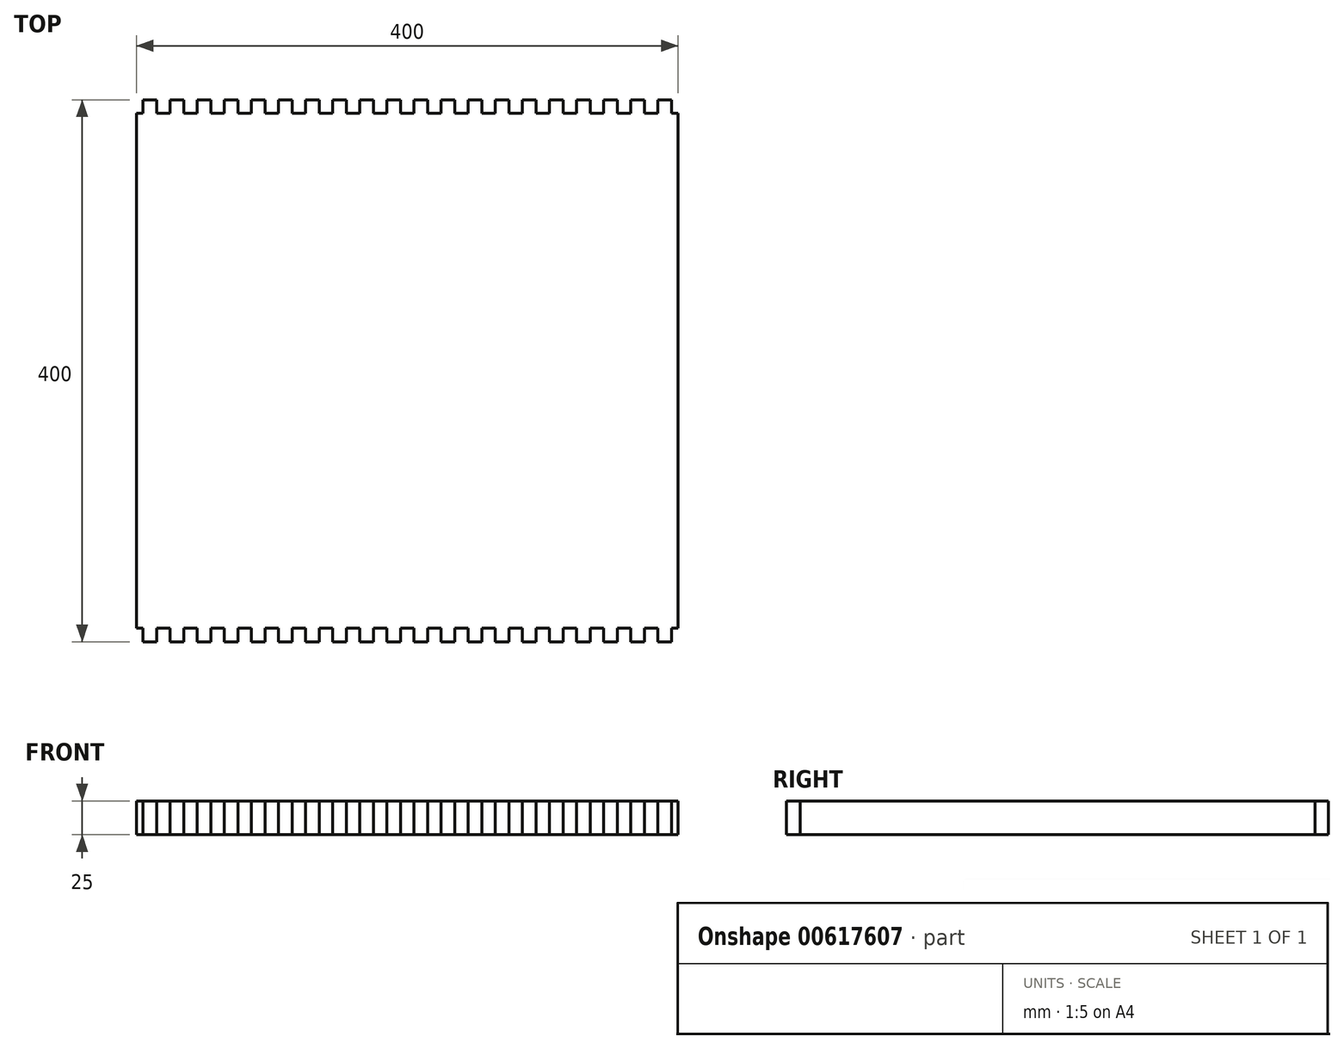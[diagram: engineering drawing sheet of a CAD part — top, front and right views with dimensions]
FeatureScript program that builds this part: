
annotation { "Feature Type Name" : "Feature", "Feature Type Description" : "" }
export const myFeature = defineFeature(function(context is Context, id is Id, definition is map)
    precondition{}
    {
        {
            var Q0;
            Q0=qCreatedBy(makeId("Top.planeOp"),FACE);
            var sketch = newSketch(context, id + "F0", { "sketchPlane" : qUnion([Q0])});
            skLineSegment(sketch, "E0.bottom", {"start": v(200, -200) * mm, "end": v(-200, -200) * mm});
            skLineSegment(sketch, "E0.top", {"start": v(200, 200) * mm, "end": v(-200, 200) * mm});
            skLineSegment(sketch, "E0.left", {"start": v(200, -200) * mm, "end": v(200, 200) * mm});
            skLineSegment(sketch, "E0.right", {"start": v(-200, -200) * mm, "end": v(-200, 200) * mm});
            skPoint(sketch, "E0.middle", {"position": v(0, 0) * mm});
            skLineSegment(sketch, "E1", {"start": v(0, -200) * mm, "end": v(-5, -200) * mm});
            skLineSegment(sketch, "E2.bottom", {"start": v(-5, -200) * mm, "end": v(5, -200) * mm});
            skLineSegment(sketch, "E2.top", {"start": v(-5, -190) * mm, "end": v(5, -190) * mm});
            skLineSegment(sketch, "E2.left", {"start": v(-5, -200) * mm, "end": v(-5, -190) * mm});
            skLineSegment(sketch, "E2.right", {"start": v(5, -200) * mm, "end": v(5, -190) * mm});
            skLineSegment(sketch, "E3.1.0.0", {"start": v(15, -190) * mm, "end": v(25, -190) * mm});
            skLineSegment(sketch, "E3.1.0.1", {"start": v(15, -200) * mm, "end": v(15, -190) * mm});
            skLineSegment(sketch, "E3.1.0.2", {"start": v(25, -200) * mm, "end": v(25, -190) * mm});
            skLineSegment(sketch, "E3.1.0.3", {"start": v(15, -200) * mm, "end": v(25, -200) * mm});
            skLineSegment(sketch, "E3.2.0.0", {"start": v(35, -190) * mm, "end": v(45, -190) * mm});
            skLineSegment(sketch, "E3.2.0.1", {"start": v(35, -200) * mm, "end": v(35, -190) * mm});
            skLineSegment(sketch, "E3.2.0.2", {"start": v(45, -200) * mm, "end": v(45, -190) * mm});
            skLineSegment(sketch, "E3.2.0.3", {"start": v(35, -200) * mm, "end": v(45, -200) * mm});
            skLineSegment(sketch, "E3.3.0.0", {"start": v(55, -190) * mm, "end": v(65, -190) * mm});
            skLineSegment(sketch, "E3.3.0.1", {"start": v(55, -200) * mm, "end": v(55, -190) * mm});
            skLineSegment(sketch, "E3.3.0.2", {"start": v(65, -200) * mm, "end": v(65, -190) * mm});
            skLineSegment(sketch, "E3.3.0.3", {"start": v(55, -200) * mm, "end": v(65, -200) * mm});
            skLineSegment(sketch, "E3.4.0.0", {"start": v(75, -190) * mm, "end": v(85, -190) * mm});
            skLineSegment(sketch, "E3.4.0.1", {"start": v(75, -200) * mm, "end": v(75, -190) * mm});
            skLineSegment(sketch, "E3.4.0.2", {"start": v(85, -200) * mm, "end": v(85, -190) * mm});
            skLineSegment(sketch, "E3.4.0.3", {"start": v(75, -200) * mm, "end": v(85, -200) * mm});
            skLineSegment(sketch, "E3.5.0.0", {"start": v(95, -190) * mm, "end": v(105, -190) * mm});
            skLineSegment(sketch, "E3.5.0.1", {"start": v(95, -200) * mm, "end": v(95, -190) * mm});
            skLineSegment(sketch, "E3.5.0.2", {"start": v(105, -200) * mm, "end": v(105, -190) * mm});
            skLineSegment(sketch, "E3.5.0.3", {"start": v(95, -200) * mm, "end": v(105, -200) * mm});
            skLineSegment(sketch, "E3.6.0.0", {"start": v(115, -190) * mm, "end": v(125, -190) * mm});
            skLineSegment(sketch, "E3.6.0.1", {"start": v(115, -200) * mm, "end": v(115, -190) * mm});
            skLineSegment(sketch, "E3.6.0.2", {"start": v(125, -200) * mm, "end": v(125, -190) * mm});
            skLineSegment(sketch, "E3.6.0.3", {"start": v(115, -200) * mm, "end": v(125, -200) * mm});
            skLineSegment(sketch, "E3.7.0.0", {"start": v(135, -190) * mm, "end": v(145, -190) * mm});
            skLineSegment(sketch, "E3.7.0.1", {"start": v(135, -200) * mm, "end": v(135, -190) * mm});
            skLineSegment(sketch, "E3.7.0.2", {"start": v(145, -200) * mm, "end": v(145, -190) * mm});
            skLineSegment(sketch, "E3.7.0.3", {"start": v(135, -200) * mm, "end": v(145, -200) * mm});
            skLineSegment(sketch, "E3.8.0.0", {"start": v(155, -190) * mm, "end": v(165, -190) * mm});
            skLineSegment(sketch, "E3.8.0.1", {"start": v(155, -200) * mm, "end": v(155, -190) * mm});
            skLineSegment(sketch, "E3.8.0.2", {"start": v(165, -200) * mm, "end": v(165, -190) * mm});
            skLineSegment(sketch, "E3.8.0.3", {"start": v(155, -200) * mm, "end": v(165, -200) * mm});
            skLineSegment(sketch, "E3.9.0.0", {"start": v(175, -190) * mm, "end": v(185, -190) * mm});
            skLineSegment(sketch, "E3.9.0.1", {"start": v(175, -200) * mm, "end": v(175, -190) * mm});
            skLineSegment(sketch, "E3.9.0.2", {"start": v(185, -200) * mm, "end": v(185, -190) * mm});
            skLineSegment(sketch, "E3.9.0.3", {"start": v(175, -200) * mm, "end": v(185, -200) * mm});
            skLineSegment(sketch, "E3.10.0.0", {"start": v(195, -190) * mm, "end": v(205, -190) * mm});
            skLineSegment(sketch, "E3.10.0.1", {"start": v(195, -200) * mm, "end": v(195, -190) * mm});
            skLineSegment(sketch, "E3.10.0.2", {"start": v(205, -200) * mm, "end": v(205, -190) * mm});
            skLineSegment(sketch, "E3.10.0.3", {"start": v(195, -200) * mm, "end": v(205, -200) * mm});
            skLineSegment(sketch, "E4.1.0.0", {"start": v(-25, -200) * mm, "end": v(-25, -190) * mm});
            skLineSegment(sketch, "E4.1.0.1", {"start": v(-25, -190) * mm, "end": v(-15, -190) * mm});
            skLineSegment(sketch, "E4.1.0.2", {"start": v(-15, -200) * mm, "end": v(-15, -190) * mm});
            skLineSegment(sketch, "E4.1.0.3", {"start": v(-25, -200) * mm, "end": v(-15, -200) * mm});
            skLineSegment(sketch, "E4.2.0.0", {"start": v(-45, -200) * mm, "end": v(-45, -190) * mm});
            skLineSegment(sketch, "E4.2.0.1", {"start": v(-45, -190) * mm, "end": v(-35, -190) * mm});
            skLineSegment(sketch, "E4.2.0.2", {"start": v(-35, -200) * mm, "end": v(-35, -190) * mm});
            skLineSegment(sketch, "E4.2.0.3", {"start": v(-45, -200) * mm, "end": v(-35, -200) * mm});
            skLineSegment(sketch, "E4.3.0.0", {"start": v(-65, -200) * mm, "end": v(-65, -190) * mm});
            skLineSegment(sketch, "E4.3.0.1", {"start": v(-65, -190) * mm, "end": v(-55, -190) * mm});
            skLineSegment(sketch, "E4.3.0.2", {"start": v(-55, -200) * mm, "end": v(-55, -190) * mm});
            skLineSegment(sketch, "E4.3.0.3", {"start": v(-65, -200) * mm, "end": v(-55, -200) * mm});
            skLineSegment(sketch, "E4.4.0.0", {"start": v(-85, -200) * mm, "end": v(-85, -190) * mm});
            skLineSegment(sketch, "E4.4.0.1", {"start": v(-85, -190) * mm, "end": v(-75, -190) * mm});
            skLineSegment(sketch, "E4.4.0.2", {"start": v(-75, -200) * mm, "end": v(-75, -190) * mm});
            skLineSegment(sketch, "E4.4.0.3", {"start": v(-85, -200) * mm, "end": v(-75, -200) * mm});
            skLineSegment(sketch, "E4.5.0.0", {"start": v(-105, -200) * mm, "end": v(-105, -190) * mm});
            skLineSegment(sketch, "E4.5.0.1", {"start": v(-105, -190) * mm, "end": v(-95, -190) * mm});
            skLineSegment(sketch, "E4.5.0.2", {"start": v(-95, -200) * mm, "end": v(-95, -190) * mm});
            skLineSegment(sketch, "E4.5.0.3", {"start": v(-105, -200) * mm, "end": v(-95, -200) * mm});
            skLineSegment(sketch, "E4.6.0.0", {"start": v(-125, -200) * mm, "end": v(-125, -190) * mm});
            skLineSegment(sketch, "E4.6.0.1", {"start": v(-125, -190) * mm, "end": v(-115, -190) * mm});
            skLineSegment(sketch, "E4.6.0.2", {"start": v(-115, -200) * mm, "end": v(-115, -190) * mm});
            skLineSegment(sketch, "E4.6.0.3", {"start": v(-125, -200) * mm, "end": v(-115, -200) * mm});
            skLineSegment(sketch, "E4.7.0.0", {"start": v(-145, -200) * mm, "end": v(-145, -190) * mm});
            skLineSegment(sketch, "E4.7.0.1", {"start": v(-145, -190) * mm, "end": v(-135, -190) * mm});
            skLineSegment(sketch, "E4.7.0.2", {"start": v(-135, -200) * mm, "end": v(-135, -190) * mm});
            skLineSegment(sketch, "E4.7.0.3", {"start": v(-145, -200) * mm, "end": v(-135, -200) * mm});
            skLineSegment(sketch, "E4.8.0.0", {"start": v(-165, -200) * mm, "end": v(-165, -190) * mm});
            skLineSegment(sketch, "E4.8.0.1", {"start": v(-165, -190) * mm, "end": v(-155, -190) * mm});
            skLineSegment(sketch, "E4.8.0.2", {"start": v(-155, -200) * mm, "end": v(-155, -190) * mm});
            skLineSegment(sketch, "E4.8.0.3", {"start": v(-165, -200) * mm, "end": v(-155, -200) * mm});
            skLineSegment(sketch, "E4.9.0.0", {"start": v(-185, -200) * mm, "end": v(-185, -190) * mm});
            skLineSegment(sketch, "E4.9.0.1", {"start": v(-185, -190) * mm, "end": v(-175, -190) * mm});
            skLineSegment(sketch, "E4.9.0.2", {"start": v(-175, -200) * mm, "end": v(-175, -190) * mm});
            skLineSegment(sketch, "E4.9.0.3", {"start": v(-185, -200) * mm, "end": v(-175, -200) * mm});
            skLineSegment(sketch, "E4.10.0.0", {"start": v(-205, -200) * mm, "end": v(-205, -190) * mm});
            skLineSegment(sketch, "E4.10.0.1", {"start": v(-205, -190) * mm, "end": v(-195, -190) * mm});
            skLineSegment(sketch, "E4.10.0.2", {"start": v(-195, -200) * mm, "end": v(-195, -190) * mm});
            skLineSegment(sketch, "E4.10.0.3", {"start": v(-205, -200) * mm, "end": v(-195, -200) * mm});
            skLineSegment(sketch, "E4.direction1", {"start": v(-5, -200) * mm, "end": v(-25, -200) * mm, "construction": true});
            skLineSegment(sketch, "E5.MirrorCS", {"start": v(-135, 200) * mm, "end": v(-135, 190) * mm});
            skLineSegment(sketch, "E6.MirrorCS", {"start": v(-125, 200) * mm, "end": v(-115, 200) * mm});
            skLineSegment(sketch, "E7.MirrorCS", {"start": v(-105, 200) * mm, "end": v(-105, 190) * mm});
            skLineSegment(sketch, "E8.MirrorCS", {"start": v(-55, 200) * mm, "end": v(-55, 190) * mm});
            skLineSegment(sketch, "E9.MirrorCS", {"start": v(-25, 200) * mm, "end": v(-25, 190) * mm});
            skLineSegment(sketch, "E10.MirrorCS", {"start": v(-145, 200) * mm, "end": v(-145, 190) * mm});
            skLineSegment(sketch, "E11.MirrorCS", {"start": v(-65, 200) * mm, "end": v(-65, 190) * mm});
            skLineSegment(sketch, "E12.MirrorCS", {"start": v(75, 200) * mm, "end": v(85, 200) * mm});
            skLineSegment(sketch, "E13.MirrorCS", {"start": v(-105, 190) * mm, "end": v(-95, 190) * mm});
            skLineSegment(sketch, "E14.MirrorCS", {"start": v(185, 200) * mm, "end": v(185, 190) * mm});
            skLineSegment(sketch, "E15.MirrorCS", {"start": v(-25, 190) * mm, "end": v(-15, 190) * mm});
            skLineSegment(sketch, "E16.MirrorCS", {"start": v(-85, 190) * mm, "end": v(-75, 190) * mm});
            skLineSegment(sketch, "E17.MirrorCS", {"start": v(195, 200) * mm, "end": v(195, 190) * mm});
            skLineSegment(sketch, "E18.MirrorCS", {"start": v(105, 200) * mm, "end": v(105, 190) * mm});
            skLineSegment(sketch, "E19.MirrorCS", {"start": v(135, 200) * mm, "end": v(135, 190) * mm});
            skLineSegment(sketch, "E20.MirrorCS", {"start": v(155, 200) * mm, "end": v(155, 190) * mm});
            skLineSegment(sketch, "E21.MirrorCS", {"start": v(-45, 190) * mm, "end": v(-35, 190) * mm});
            skLineSegment(sketch, "E22.MirrorCS", {"start": v(55, 200) * mm, "end": v(65, 200) * mm});
            skLineSegment(sketch, "E23.MirrorCS", {"start": v(75, 200) * mm, "end": v(75, 190) * mm});
            skLineSegment(sketch, "E24.MirrorCS", {"start": v(-125, 190) * mm, "end": v(-115, 190) * mm});
            skLineSegment(sketch, "E25.MirrorCS", {"start": v(-165, 200) * mm, "end": v(-165, 190) * mm});
            skLineSegment(sketch, "E26.MirrorCS", {"start": v(175, 200) * mm, "end": v(175, 190) * mm});
            skLineSegment(sketch, "E27.MirrorCS", {"start": v(-155, 200) * mm, "end": v(-155, 190) * mm});
            skLineSegment(sketch, "E28.MirrorCS", {"start": v(-105, 200) * mm, "end": v(-95, 200) * mm});
            skLineSegment(sketch, "E29.MirrorCS", {"start": v(-75, 200) * mm, "end": v(-75, 190) * mm});
            skLineSegment(sketch, "E30.MirrorCS", {"start": v(-85, 200) * mm, "end": v(-85, 190) * mm});
            skLineSegment(sketch, "E31.MirrorCS", {"start": v(125, 200) * mm, "end": v(125, 190) * mm});
            skLineSegment(sketch, "E32.MirrorCS", {"start": v(-25, 200) * mm, "end": v(-15, 200) * mm});
            skLineSegment(sketch, "E33.MirrorCS", {"start": v(135, 200) * mm, "end": v(145, 200) * mm});
            skLineSegment(sketch, "E34.MirrorCS", {"start": v(-35, 200) * mm, "end": v(-35, 190) * mm});
            skLineSegment(sketch, "E35.MirrorCS", {"start": v(165, 200) * mm, "end": v(165, 190) * mm});
            skLineSegment(sketch, "E36.MirrorCS", {"start": v(85, 200) * mm, "end": v(85, 190) * mm});
            skLineSegment(sketch, "E37.MirrorCS", {"start": v(-115, 200) * mm, "end": v(-115, 190) * mm});
            skLineSegment(sketch, "E38.MirrorCS", {"start": v(-85, 200) * mm, "end": v(-75, 200) * mm});
            skLineSegment(sketch, "E39.MirrorCS", {"start": v(-65, 190) * mm, "end": v(-55, 190) * mm});
            skLineSegment(sketch, "E40.MirrorCS", {"start": v(55, 200) * mm, "end": v(55, 190) * mm});
            skLineSegment(sketch, "E41.MirrorCS", {"start": v(-5, 200) * mm, "end": v(5, 200) * mm});
            skLineSegment(sketch, "E42.MirrorCS", {"start": v(0, 200) * mm, "end": v(-5, 200) * mm});
            skLineSegment(sketch, "E43.MirrorCS", {"start": v(-145, 190) * mm, "end": v(-135, 190) * mm});
            skLineSegment(sketch, "E44.MirrorCS", {"start": v(-125, 200) * mm, "end": v(-125, 190) * mm});
            skLineSegment(sketch, "E45.MirrorCS", {"start": v(155, 190) * mm, "end": v(165, 190) * mm});
            skLineSegment(sketch, "E46.MirrorCS", {"start": v(75, 190) * mm, "end": v(85, 190) * mm});
            skLineSegment(sketch, "E47.MirrorCS", {"start": v(-45, 200) * mm, "end": v(-45, 190) * mm});
            skLineSegment(sketch, "E48.MirrorCS", {"start": v(55, 190) * mm, "end": v(65, 190) * mm});
            skLineSegment(sketch, "E49.MirrorCS", {"start": v(-185, 200) * mm, "end": v(-185, 190) * mm});
            skLineSegment(sketch, "E50.MirrorCS", {"start": v(-65, 200) * mm, "end": v(-55, 200) * mm});
            skLineSegment(sketch, "E51.MirrorCS", {"start": v(-95, 200) * mm, "end": v(-95, 190) * mm});
            skLineSegment(sketch, "E52.MirrorCS", {"start": v(175, 200) * mm, "end": v(185, 200) * mm});
            skLineSegment(sketch, "E53.MirrorCS", {"start": v(-15, 200) * mm, "end": v(-15, 190) * mm});
            skLineSegment(sketch, "E54.MirrorCS", {"start": v(145, 200) * mm, "end": v(145, 190) * mm});
            skLineSegment(sketch, "E55.MirrorCS", {"start": v(95, 200) * mm, "end": v(105, 200) * mm});
            skLineSegment(sketch, "E56.MirrorCS", {"start": v(-5, 200) * mm, "end": v(-5, 190) * mm});
            skLineSegment(sketch, "E57.MirrorCS", {"start": v(135, 190) * mm, "end": v(145, 190) * mm});
            skLineSegment(sketch, "E58.MirrorCS", {"start": v(-5, 200) * mm, "end": v(-25, 200) * mm, "construction": true});
            skLineSegment(sketch, "E59.MirrorCS", {"start": v(95, 190) * mm, "end": v(105, 190) * mm});
            skLineSegment(sketch, "E60.MirrorCS", {"start": v(175, 190) * mm, "end": v(185, 190) * mm});
            skLineSegment(sketch, "E61.MirrorCS", {"start": v(-145, 200) * mm, "end": v(-135, 200) * mm});
            skLineSegment(sketch, "E62.MirrorCS", {"start": v(25, 200) * mm, "end": v(25, 190) * mm});
            skLineSegment(sketch, "E63.MirrorCS", {"start": v(-45, 200) * mm, "end": v(-35, 200) * mm});
            skLineSegment(sketch, "E64.MirrorCS", {"start": v(65, 200) * mm, "end": v(65, 190) * mm});
            skLineSegment(sketch, "E65.MirrorCS", {"start": v(155, 200) * mm, "end": v(165, 200) * mm});
            skLineSegment(sketch, "E66.MirrorCS", {"start": v(95, 200) * mm, "end": v(95, 190) * mm});
            skLineSegment(sketch, "E67.MirrorCS", {"start": v(-5, 190) * mm, "end": v(5, 190) * mm});
            skLineSegment(sketch, "E68.MirrorCS", {"start": v(35, 200) * mm, "end": v(35, 190) * mm});
            skLineSegment(sketch, "E69.MirrorCS", {"start": v(-165, 190) * mm, "end": v(-155, 190) * mm});
            skLineSegment(sketch, "E70.MirrorCS", {"start": v(115, 200) * mm, "end": v(115, 190) * mm});
            skLineSegment(sketch, "E71.MirrorCS", {"start": v(45, 200) * mm, "end": v(45, 190) * mm});
            skLineSegment(sketch, "E72.MirrorCS", {"start": v(-185, 200) * mm, "end": v(-175, 200) * mm});
            skLineSegment(sketch, "E73.MirrorCS", {"start": v(195, 190) * mm, "end": v(205, 190) * mm});
            skLineSegment(sketch, "E74.MirrorCS", {"start": v(115, 190) * mm, "end": v(125, 190) * mm});
            skLineSegment(sketch, "E75.MirrorCS", {"start": v(-185, 190) * mm, "end": v(-175, 190) * mm});
            skLineSegment(sketch, "E76.MirrorCS", {"start": v(35, 200) * mm, "end": v(45, 200) * mm});
            skLineSegment(sketch, "E77.MirrorCS", {"start": v(-165, 200) * mm, "end": v(-155, 200) * mm});
            skLineSegment(sketch, "E78.MirrorCS", {"start": v(115, 200) * mm, "end": v(125, 200) * mm});
            skLineSegment(sketch, "E79.MirrorCS", {"start": v(-175, 200) * mm, "end": v(-175, 190) * mm});
            skLineSegment(sketch, "E80.MirrorCS", {"start": v(15, 200) * mm, "end": v(15, 190) * mm});
            skLineSegment(sketch, "E81.MirrorCS", {"start": v(15, 190) * mm, "end": v(25, 190) * mm});
            skLineSegment(sketch, "E82.MirrorCS", {"start": v(5, 200) * mm, "end": v(5, 190) * mm});
            skLineSegment(sketch, "E83.MirrorCS", {"start": v(35, 190) * mm, "end": v(45, 190) * mm});
            skLineSegment(sketch, "E84.MirrorCS", {"start": v(15, 200) * mm, "end": v(25, 200) * mm});
            skLineSegment(sketch, "E85.MirrorCS", {"start": v(205, 200) * mm, "end": v(205, 190) * mm});
            skLineSegment(sketch, "E86.MirrorCS", {"start": v(195, 200) * mm, "end": v(205, 200) * mm});
            skLineSegment(sketch, "E87.MirrorCS", {"start": v(-205, 200) * mm, "end": v(-195, 200) * mm});
            skLineSegment(sketch, "E88.MirrorCS", {"start": v(-205, 190) * mm, "end": v(-195, 190) * mm});
            skLineSegment(sketch, "E89.MirrorCS", {"start": v(-195, 200) * mm, "end": v(-195, 190) * mm});
            skLineSegment(sketch, "E90.MirrorCS", {"start": v(-205, 200) * mm, "end": v(-205, 190) * mm});
            skSolve(sketch);
        }
        {
            var Q0;
            Q0=makeQuery(id+"F0.imprint","IMPRINT",FACE,{"disambiguationData":[TD([[makeQuery(id+"F0.imprint","IMPRINT",EDGE,{"derivedFrom":sQuery(id+"F0.wireOp",EDGE,"E2.top")}),1.0]])]});
            extrude(context, id + "F1", {"entities" : qUnion([Q0]), "depth" : 25 * mm, "offsetDistance" : 25 * mm});
        }
    });
